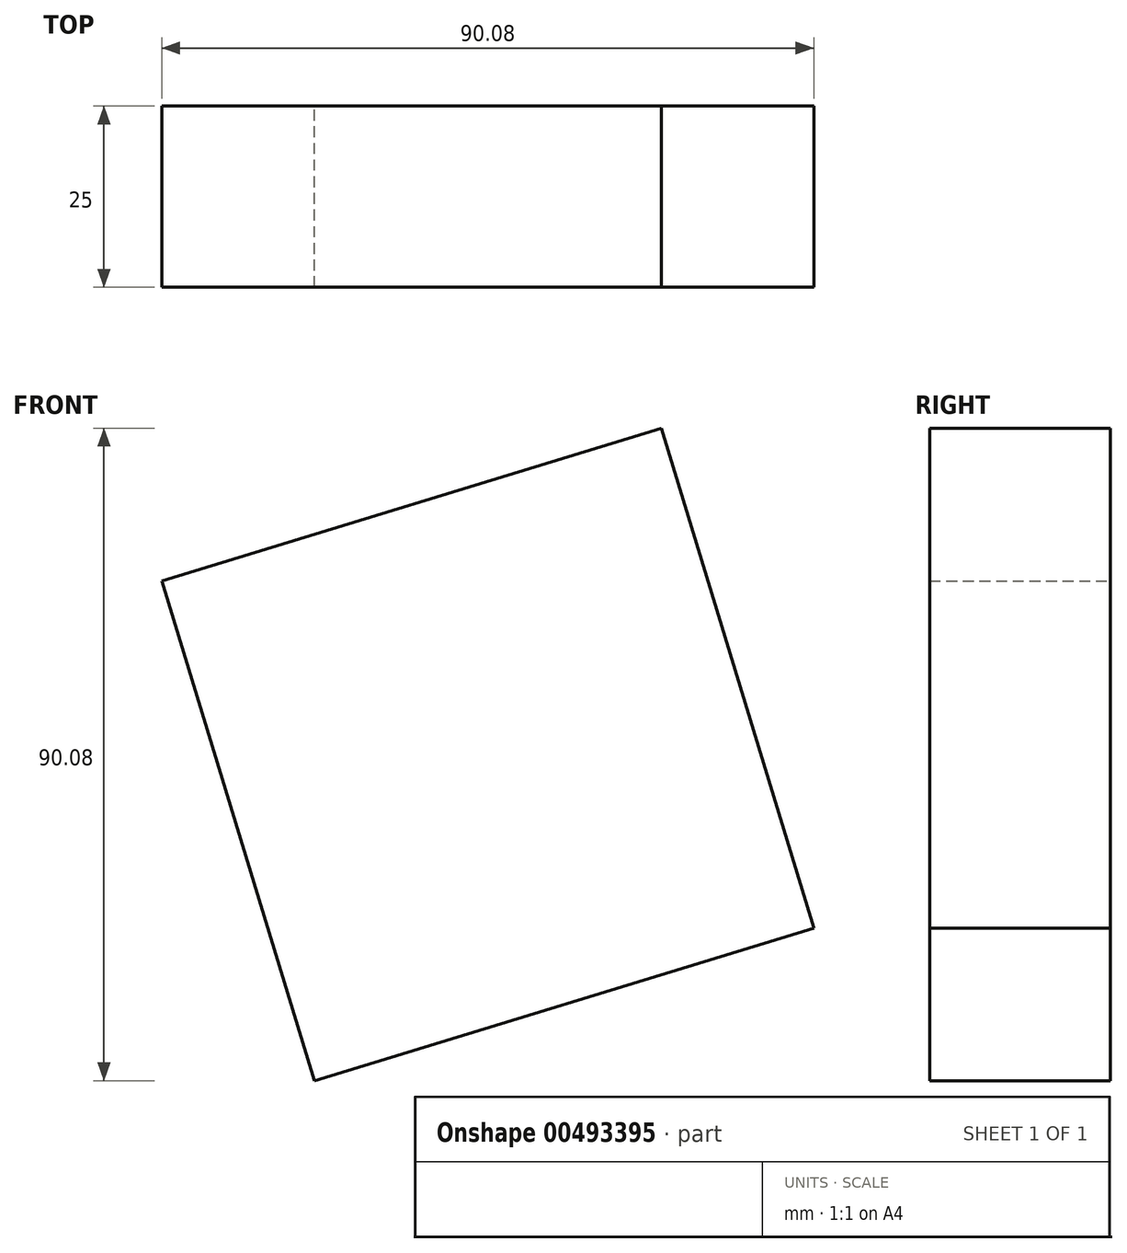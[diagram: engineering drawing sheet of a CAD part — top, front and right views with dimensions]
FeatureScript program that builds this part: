
annotation { "Feature Type Name" : "Feature", "Feature Type Description" : "" }
export const myFeature = defineFeature(function(context is Context, id is Id, definition is map)
    precondition{}
    {
        {
            var Q0;
            Q0=qCreatedBy(makeId("Front.planeOp"),FACE);
            var sketch = newSketch(context, id + "F0", { "sketchPlane" : qUnion([Q0])});
            skCircle(sketch, "E0.cCircle", {"center": v(0, 0) * mm, "radius": 51.01 * mm, "construction": true});
            skLineSegment(sketch, "E0.0", {"start": v(-45.04, 23.95) * mm, "end": v(23.95, 45.04) * mm});
            skLineSegment(sketch, "E0.1", {"start": v(23.95, 45.04) * mm, "end": v(45.04, -23.95) * mm});
            skLineSegment(sketch, "E0.2", {"start": v(45.04, -23.95) * mm, "end": v(-23.95, -45.04) * mm});
            skLineSegment(sketch, "E0.3", {"start": v(-23.95, -45.04) * mm, "end": v(-45.04, 23.95) * mm});
            skSolve(sketch);
        }
        {
            var Q0;
            Q0 = qSketchRegion(id + "F0", true);
            extrude(context, id + "F1", {"entities" : qUnion([Q0]), "depth" : 25 * mm});
        }
    });
